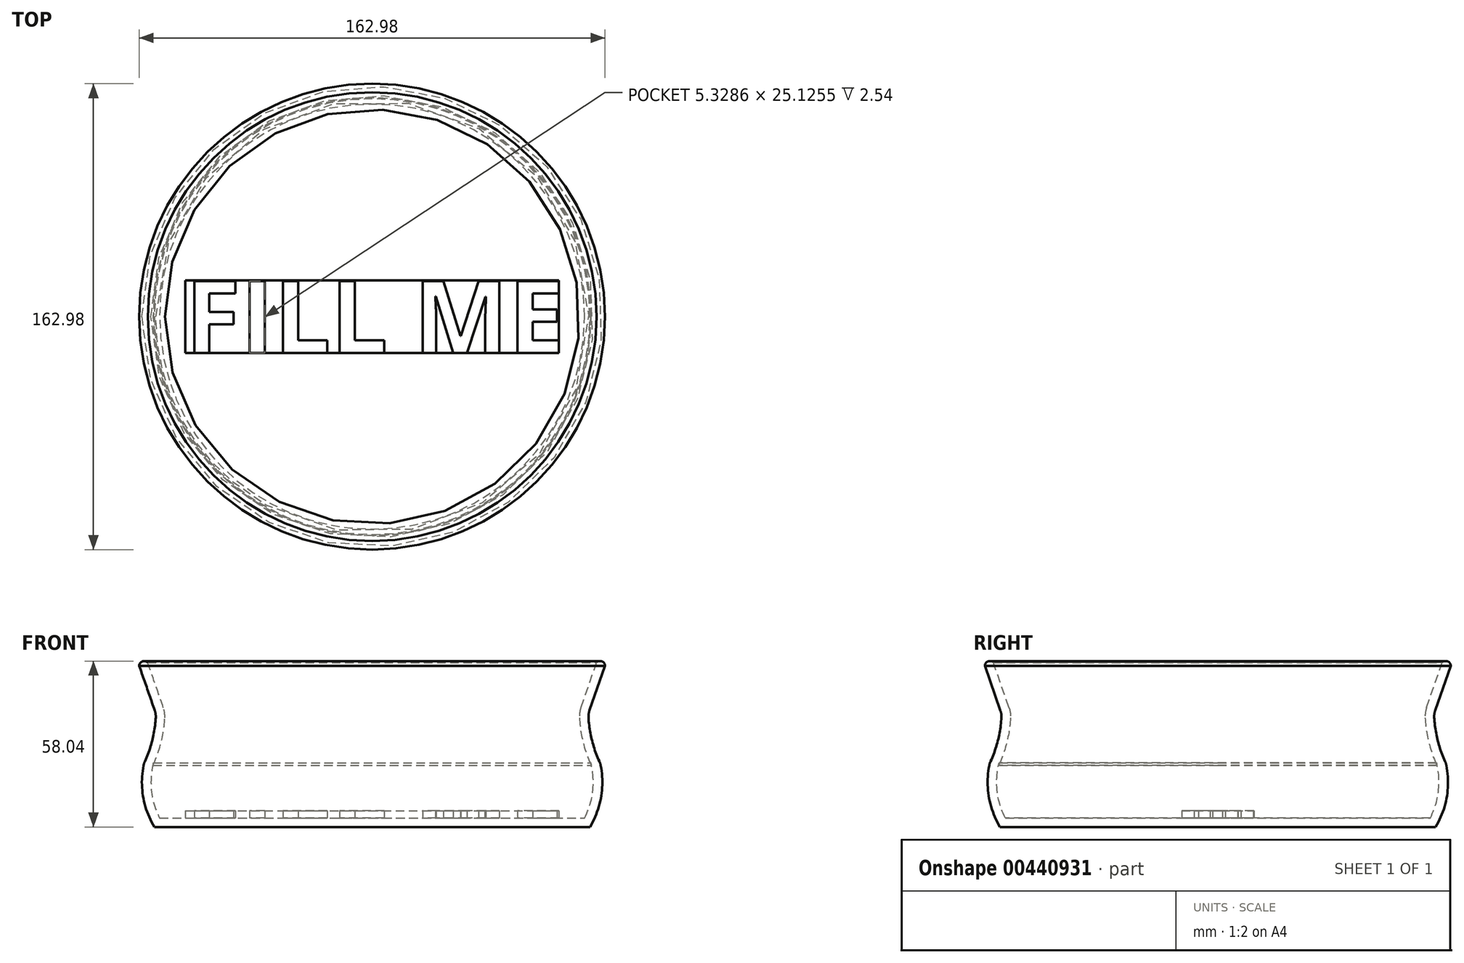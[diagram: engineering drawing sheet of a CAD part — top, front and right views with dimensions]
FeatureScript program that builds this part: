
annotation { "Feature Type Name" : "Feature", "Feature Type Description" : "" }
export const myFeature = defineFeature(function(context is Context, id is Id, definition is map)
    precondition{}
    {
        {
            var Q0;
            Q0=qCreatedBy(makeId("Front.planeOp"),FACE);
            var sketch = newSketch(context, id + "F0", { "sketchPlane" : qUnion([Q0])});
            skLineSegment(sketch, "E0", {"start": v(0, 0) * mm, "end": v(-76.2, 0) * mm});
            skArc(sketch, "E1", {"start": v(-79.97, 21.5) * mm, "mid": v(-80.09, 10.4) * mm, "end": v(-76.2, 0) * mm});
            skArc(sketch, "E2", {"start": v(-79.5, 22.93) * mm, "mid": v(-76.87, 30.45) * mm, "end": v(-75.7, 38.34) * mm});
            skLineSegment(sketch, "E3", {"start": v(-76.05, 40.75) * mm, "end": v(-81.5, 56.4) * mm});
            skPoint(sketch, "E4.visualSharp", {"position": v(-40.76, 41) * mm});
            skPoint(sketch, "E5.visualSharp", {"position": v(-75.66, 39.63) * mm});
            skArc(sketch, "E5.filletArc", {"start": v(-75.7, 38.34) * mm, "mid": v(-75.76, 39.56) * mm, "end": v(-76.05, 40.75) * mm});
            skPoint(sketch, "E6.visualSharp", {"position": v(-79.8, 22.3) * mm});
            skArc(sketch, "E6.filletArc", {"start": v(-79.5, 22.93) * mm, "mid": v(-79.78, 22.23) * mm, "end": v(-79.97, 21.5) * mm});
            skPoint(sketch, "E7.visualSharp", {"position": v(-45.27, 23.26) * mm});
            skArc(sketch, "E8.0", {"start": v(-76.5, 22.42) * mm, "mid": v(-77.2, 12.6) * mm, "end": v(-74.34, 3.17) * mm});
            skLineSegment(sketch, "E9", {"start": v(-74.34, 3.17) * mm, "end": v(0, 3.17) * mm});
            skLineSegment(sketch, "E10", {"start": v(0, 0) * mm, "end": v(0, 3.17) * mm});
            skArc(sketch, "E11.0", {"start": v(-76.62, 21.6) * mm, "mid": v(-73.79, 29.7) * mm, "end": v(-72.54, 38.18) * mm});
            skArc(sketch, "E12", {"start": v(-76.62, 21.6) * mm, "mid": v(-76.55, 22) * mm, "end": v(-76.5, 22.42) * mm});
            skLineSegment(sketch, "E13.0", {"start": v(-73.05, 41.8) * mm, "end": v(-78.5, 57.44) * mm});
            skArc(sketch, "E14", {"start": v(-72.54, 38.18) * mm, "mid": v(-72.62, 40.01) * mm, "end": v(-73.05, 41.8) * mm});
            skArc(sketch, "E15", {"start": v(-78.5, 57.44) * mm, "mid": v(-80.35, 57.95) * mm, "end": v(-81.5, 56.4) * mm});
            skSolve(sketch);
        }
        {
            var Q0;
            Q0=makeQuery(id+"F0.imprint","IMPRINT",FACE,{"disambiguationData":[TD([[makeQuery(id+"F0.imprint","IMPRINT",EDGE,{"derivedFrom":sQuery(id+"F0.wireOp",EDGE,"E0")}),-1.0]])]});
            var Q1;
            Q1=sQuery(id+"F0.wireOp",EDGE,"E10");
            revolve(context, id + "F1", {"entities" : qUnion([Q0]), "axis" : qUnion([Q1]), "revolveType" : RevolveType.FULL});
        }
        {
            var Q0;
            Q0=makeQuery(id+"F1.opRevolve","SWEPT_FACE",FACE,{"disambiguationData":[OSD([sQuery(id+"F0.wireOp",EDGE,"E9")])]});
            var sketch = newSketch(context, id + "F2", { "sketchPlane" : qUnion([Q0])});
            skLineSegment(sketch, "E16.rect.bottom", {"start": v(-65.36, 12.67) * mm, "end": v(65.36, 12.67) * mm});
            skLineSegment(sketch, "E16.rect.top", {"start": v(-65.36, -12.67) * mm, "end": v(65.36, -12.67) * mm});
            skLineSegment(sketch, "E16.rect.left", {"start": v(-65.36, 12.67) * mm, "end": v(-65.36, -12.67) * mm});
            skLineSegment(sketch, "E16.rect.right", {"start": v(65.36, 12.67) * mm, "end": v(65.36, -12.67) * mm});
            skPoint(sketch, "E16.rect.middle", {"position": v(0, 0) * mm});
            skText(sketch, "E17", { "text": "FILL ME", "fontName": "OpenSans-Bold.ttf"});
            const initialGuessF2  = {"E17": [-0.06536, -0.01267, 1, 0, 0.02534]};
            skSetInitialGuess(sketch, initialGuessF2);
            skSolve(sketch);
        }
        {
            var Q0;
            Q0=qSketchRegion(id+"F2",true);
            extrude(context, id + "F3", {"entities" : qUnion([Q0]), "operationType" : NewBodyOperationType.ADD, "depth" : 2.54 * mm});
        }
    });
